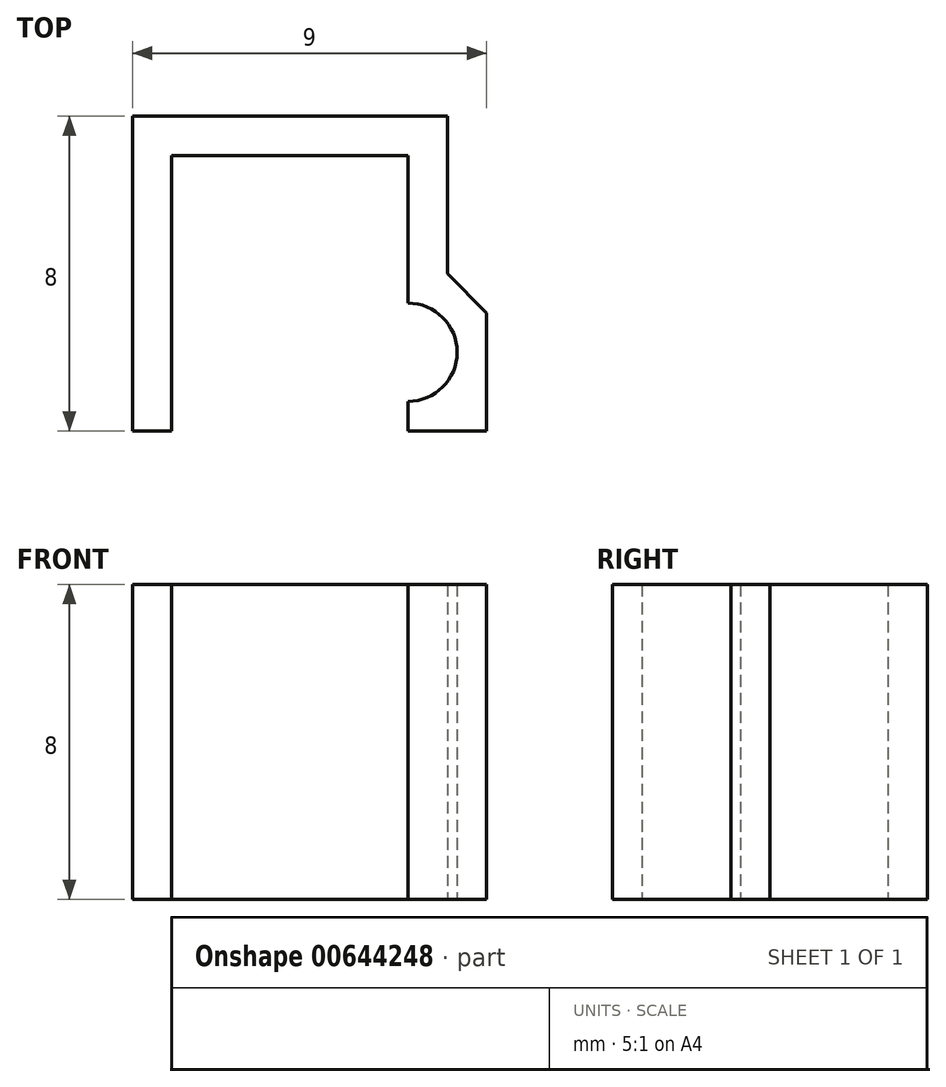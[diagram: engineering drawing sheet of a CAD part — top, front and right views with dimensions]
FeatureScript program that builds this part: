
annotation { "Feature Type Name" : "Feature", "Feature Type Description" : "" }
export const myFeature = defineFeature(function(context is Context, id is Id, definition is map)
    precondition{}
    {
        {
            var Q0;
            Q0=qCreatedBy(makeId("Top.planeOp"),FACE);
            var sketch = newSketch(context, id + "F0", { "sketchPlane" : qUnion([Q0])});
            skLineSegment(sketch, "E0.bottom", {"start": v(-2.5, 3) * mm, "end": v(3.5, 3) * mm});
            skLineSegment(sketch, "E0.top", {"start": v(-2.5, -4) * mm, "end": v(3.5, -4) * mm});
            skLineSegment(sketch, "E0.left", {"start": v(-2.5, 3) * mm, "end": v(-2.5, -4) * mm});
            skLineSegment(sketch, "E0.right", {"start": v(3.5, 3) * mm, "end": v(3.5, -4) * mm});
            skPoint(sketch, "E0.middle", {"position": v(0.5, 0) * mm});
            skLineSegment(sketch, "E1.bottom", {"start": v(4.5, -4) * mm, "end": v(-3.5, -4) * mm});
            skLineSegment(sketch, "E1.top", {"start": v(4.5, 4) * mm, "end": v(-3.5, 4) * mm});
            skLineSegment(sketch, "E1.left", {"start": v(4.5, -4) * mm, "end": v(4.5, 4) * mm});
            skLineSegment(sketch, "E1.right", {"start": v(-3.5, -4) * mm, "end": v(-3.5, 4) * mm});
            skLineSegment(sketch, "E2", {"start": v(-2.5, -4) * mm, "end": v(-2.5, -3) * mm});
            skLineSegment(sketch, "E3", {"start": v(-2.5, -3) * mm, "end": v(-1.5, -4) * mm});
            skLineSegment(sketch, "E4", {"start": v(4.5, 0) * mm, "end": v(5.5, -1) * mm});
            skLineSegment(sketch, "E5", {"start": v(5.5, -1) * mm, "end": v(5.5, -4) * mm});
            skLineSegment(sketch, "E6", {"start": v(5.5, -4) * mm, "end": v(4.5, -4) * mm});
            skPoint(sketch, "E7", {"position": v(3.5, -2) * mm});
            skSolve(sketch);
        }
        {
            var Q0;
            {var subQ9=sQuery(id+"F0.wireOp",EDGE,"E0.bottom");Q0=makeQuery(id+"F0.imprint","IMPRINT",FACE,{"disambiguationData":[TD([[makeQuery(id+"F0.imprint","IMPRINT",EDGE,{"derivedFrom":subQ9}),1.0]])]});}
            var Q1;
            {var subQ2=sQuery(id+"F0.wireOp",EDGE,"E4");Q1=makeQuery(id+"F0.imprint","IMPRINT",FACE,{"disambiguationData":[TD([[makeQuery(id+"F0.imprint","IMPRINT",EDGE,{"derivedFrom":subQ2}),-1.0]])]});}
            var Q2;
            {var subQ0=sQuery(id+"F0.wireOp",EDGE,"E2");Q2=makeQuery(id+"F0.imprint","IMPRINT",FACE,{"disambiguationData":[TD([[makeQuery(id+"F0.imprint","IMPRINT",EDGE,{"derivedFrom":subQ0}),-1.0]])]});}
            extrude(context, id + "F1", {"entities" : qUnion([Q0, Q1, Q2]), "depth" : 8 * mm, "offsetDistance" : 25 * mm});
        }
        {
            var Q0;
            Q0=sQuery(id+"F0.wireOp",VERTEX,"E7");
            var Q1;
            Q1=makeQuery(id+"F1.opExtrude","SWEPT_BODY",BODY,{"disambiguationData":[OSD([sQuery(id+"F0.wireOp",EDGE,"E0.bottom"),sQuery(id+"F0.wireOp",EDGE,"E0.left"),sQuery(id+"F0.wireOp",EDGE,"E0.right"),sQuery(id+"F0.wireOp",EDGE,"E1.bottom"),sQuery(id+"F0.wireOp",EDGE,"E1.top"),sQuery(id+"F0.wireOp",EDGE,"E1.left"),sQuery(id+"F0.wireOp",EDGE,"E1.right"),sQuery(id+"F0.wireOp",EDGE,"E3"),sQuery(id+"F0.wireOp",EDGE,"E4"),sQuery(id+"F0.wireOp",EDGE,"E5"),sQuery(id+"F0.wireOp",EDGE,"E6")])]});
            hole(context, id + "F2", {"style" : HoleStyle.SIMPLE, "endStyle" : HoleEndStyle.THROUGH, "oppositeDirection" : true, "holeDiameter" : 2.5 * mm, "majorDiameter" : 5 * mm, "isTappedThrough" : true, "tappedDepth" : 12 * mm, "tapClearance" : 3, "locations" : qUnion([Q0]), "scope" : qUnion([Q1])});
        }
    });
